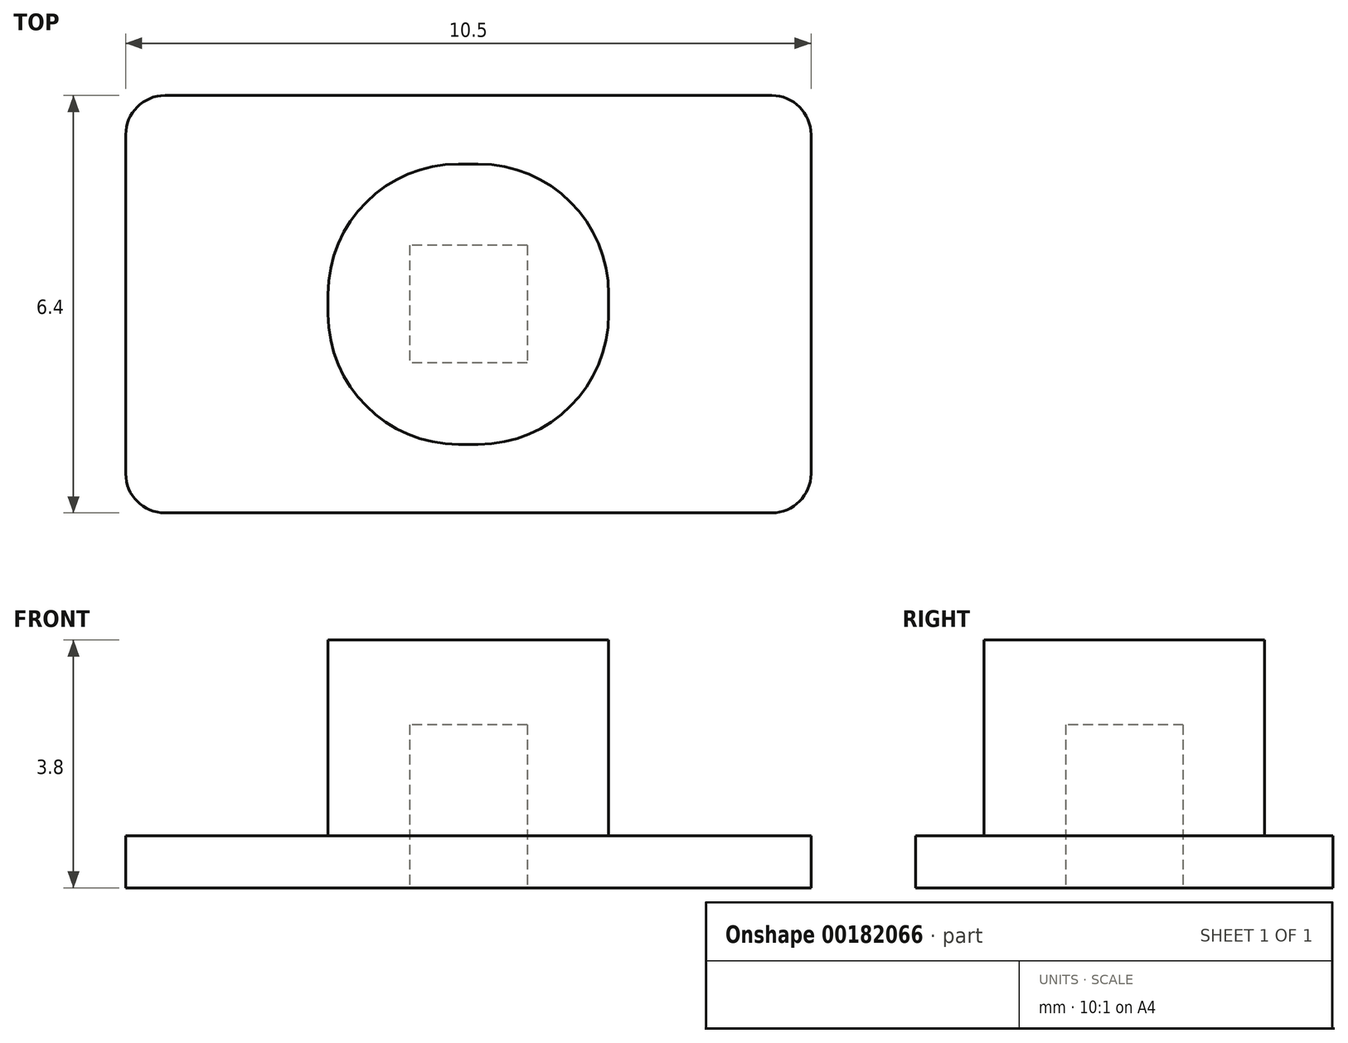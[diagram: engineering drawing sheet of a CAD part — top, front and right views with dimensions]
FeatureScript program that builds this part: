
annotation { "Feature Type Name" : "Feature", "Feature Type Description" : "" }
export const myFeature = defineFeature(function(context is Context, id is Id, definition is map)
    precondition{}
    {
        {
            var Q0;
            Q0=qCreatedBy(makeId("Top.planeOp"),FACE);
            var sketch = newSketch(context, id + "F0", { "sketchPlane" : qUnion([Q0])});
            skLineSegment(sketch, "E0.bottom", {"start": v(5.25, -3.2) * mm, "end": v(-5.25, -3.2) * mm});
            skLineSegment(sketch, "E0.top", {"start": v(5.25, 3.2) * mm, "end": v(-5.25, 3.2) * mm});
            skLineSegment(sketch, "E0.left", {"start": v(5.25, -3.2) * mm, "end": v(5.25, 3.2) * mm});
            skLineSegment(sketch, "E0.right", {"start": v(-5.25, -3.2) * mm, "end": v(-5.25, 3.2) * mm});
            skPoint(sketch, "E0.middle", {"position": v(0, 0) * mm});
            skSolve(sketch);
        }
        {
            var Q0;
            Q0 = qSketchRegion(id + "F0", true);
            extrude(context, id + "F1", {"entities" : qUnion([Q0]), "depth" : 0.8 * mm});
        }
        {
            var Q0;
            Q0=makeQuery(id+"F1.opExtrude","CAP_FACE",FACE,{"disambiguationData":[OSD([sQuery(id+"F0.wireOp",EDGE,"E0.bottom"),sQuery(id+"F0.wireOp",EDGE,"E0.top"),sQuery(id+"F0.wireOp",EDGE,"E0.left"),sQuery(id+"F0.wireOp",EDGE,"E0.right")])],"isStart":false});
            var sketch = newSketch(context, id + "F2", { "sketchPlane" : qUnion([Q0])});
            skLineSegment(sketch, "E1.bottom", {"start": v(-2.15, 2.15) * mm, "end": v(2.15, 2.15) * mm});
            skLineSegment(sketch, "E1.top", {"start": v(-2.15, -2.15) * mm, "end": v(2.15, -2.15) * mm});
            skLineSegment(sketch, "E1.left", {"start": v(-2.15, 2.15) * mm, "end": v(-2.15, -2.15) * mm});
            skLineSegment(sketch, "E1.right", {"start": v(2.15, 2.15) * mm, "end": v(2.15, -2.15) * mm});
            skPoint(sketch, "E1.middle", {"position": v(0, 0) * mm});
            skSolve(sketch);
        }
        {
            var Q0;
            Q0 = qSketchRegion(id + "F2", true);
            extrude(context, id + "F3", {"entities" : qUnion([Q0]), "operationType" : NewBodyOperationType.ADD, "depth" : 3 * mm});
        }
        {
            var Q0;
            Q0=makeQuery(id+"F3.opExtrude","SWEPT_EDGE",EDGE,{"disambiguationData":[OSD([sQuery(id+"F2.wireOp",EDGE,"E1.top"),sQuery(id+"F2.wireOp",EDGE,"E1.left")])]});
            var Q1;
            Q1=makeQuery(id+"F3.opExtrude","SWEPT_EDGE",EDGE,{"disambiguationData":[OSD([sQuery(id+"F2.wireOp",EDGE,"E1.bottom"),sQuery(id+"F2.wireOp",EDGE,"E1.left")])]});
            var Q2;
            Q2=makeQuery(id+"F3.opExtrude","SWEPT_EDGE",EDGE,{"disambiguationData":[OSD([sQuery(id+"F2.wireOp",EDGE,"E1.top"),sQuery(id+"F2.wireOp",EDGE,"E1.right")])]});
            var Q3;
            Q3=makeQuery(id+"F3.opExtrude","SWEPT_EDGE",EDGE,{"disambiguationData":[OSD([sQuery(id+"F2.wireOp",EDGE,"E1.bottom"),sQuery(id+"F2.wireOp",EDGE,"E1.right")])]});
            fillet(context, id + "F4", {"entities" : qUnion([Q0, Q1, Q2, Q3]), "radius" : 2 * mm, "tangentPropagation" : true, "allowEdgeOverflow" : false});
        }
        {
            var Q0;
            Q0=makeQuery(id+"F1.opExtrude","SWEPT_EDGE",EDGE,{"disambiguationData":[OSD([sQuery(id+"F0.wireOp",EDGE,"E0.bottom"),sQuery(id+"F0.wireOp",EDGE,"E0.right")])]});
            var Q1;
            Q1=makeQuery(id+"F1.opExtrude","SWEPT_EDGE",EDGE,{"disambiguationData":[OSD([sQuery(id+"F0.wireOp",EDGE,"E0.top"),sQuery(id+"F0.wireOp",EDGE,"E0.right")])]});
            var Q2;
            Q2=makeQuery(id+"F1.opExtrude","SWEPT_EDGE",EDGE,{"disambiguationData":[OSD([sQuery(id+"F0.wireOp",EDGE,"E0.bottom"),sQuery(id+"F0.wireOp",EDGE,"E0.left")])]});
            var Q3;
            Q3=makeQuery(id+"F1.opExtrude","SWEPT_EDGE",EDGE,{"disambiguationData":[OSD([sQuery(id+"F0.wireOp",EDGE,"E0.top"),sQuery(id+"F0.wireOp",EDGE,"E0.left")])]});
            fillet(context, id + "F5", {"entities" : qUnion([Q0, Q1, Q2, Q3]), "radius" : 0.6 * mm, "tangentPropagation" : true, "allowEdgeOverflow" : false});
        }
        {
            var Q0;
            Q0=makeQuery(id+"F1.opExtrude","CAP_FACE",FACE,{"disambiguationData":[OSD([sQuery(id+"F0.wireOp",EDGE,"E0.bottom"),sQuery(id+"F0.wireOp",EDGE,"E0.top"),sQuery(id+"F0.wireOp",EDGE,"E0.left"),sQuery(id+"F0.wireOp",EDGE,"E0.right")])],"isStart":true});
            var sketch = newSketch(context, id + "F6", { "sketchPlane" : qUnion([Q0])});
            skLineSegment(sketch, "E2.bottom", {"start": v(0.9, -0.9) * mm, "end": v(-0.9, -0.9) * mm});
            skLineSegment(sketch, "E2.top", {"start": v(0.9, 0.9) * mm, "end": v(-0.9, 0.9) * mm});
            skLineSegment(sketch, "E2.left", {"start": v(0.9, -0.9) * mm, "end": v(0.9, 0.9) * mm});
            skLineSegment(sketch, "E2.right", {"start": v(-0.9, -0.9) * mm, "end": v(-0.9, 0.9) * mm});
            skPoint(sketch, "E2.middle", {"position": v(0, 0) * mm});
            skSolve(sketch);
        }
        {
            var Q0;
            Q0 = qSketchRegion(id + "F6", true);
            extrude(context, id + "F7", {"entities" : qUnion([Q0]), "operationType" : NewBodyOperationType.REMOVE, "oppositeDirection" : true, "depth" : 2.5 * mm});
        }
    });
